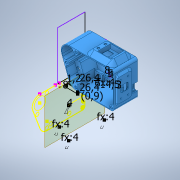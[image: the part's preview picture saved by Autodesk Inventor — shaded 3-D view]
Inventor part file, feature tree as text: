
AUTODESK INVENTOR PART (.ipt)
format: ipt  version: 2021.1 (Build 251245010, 245A)  size: 1,980,928 bytes
history: mixed  units: in
note: dims shown in document units (in); Inventor stores cm internally (conversion verified against a paired STEP export)
features: extrude x24, sketch x21, move_body x9, direct_edit x7, chamfer x6, projected_geometry x5, other x4, revolve x4, fillet x1, plane x1, imported_body x1
ambient origin geometry x8: Origin, YZ Plane, XZ Plane, XY Plane, X Axis, Y Axis, Z Axis, Center Point
bodies: Solid1 (imported_parasolid), Volumenkörper268 (imported_parasolid), Body1 (imported_parasolid)
feature tree (83):
  sketch  "Skizze1"  dims[d0=0.1575in d1=0.1575in]
  extrude  "Extrusion2"  Depth=0.1575in
  extrude  "Extrusion1"  Depth=0.1575in
  sketch  "Skizze3"  dims[d2=0.1575in d3=0.1575in]
  extrude  "Extrusion3"  Depth=0.252in TaperAngle=0.0deg
  extrude  "Extrusion4"  Depth=0.2756in TaperAngle=0.0deg
  extrude  "Extrusion5"  Depth=0.1575in
  extrude  "Extrusion6"  Depth=0.1575in
  direct_edit  "Direktbearbeitung2"
  extrude  "Extrusion8"  Depth=0.315in
  direct_edit  "Direktbearbeitung3"
  extrude  "Extrusion10"  Depth=0.1969in TaperAngle=0.0deg
  extrude  "Extrusion11"  TaperAngle=135.0deg  [1 undecoded]
  sketch  "Skizze16"  dims[d19=45.0deg d20=0.1969in d21=0.5906in d22=0.0in d23=0.0in]
  direct_edit  "Direktbearbeitung4"
  extrude  "Extrusion19"  TaperAngle=0.0deg  [1 undecoded]
  direct_edit  "Direktbearbeitung6"
  direct_edit  "Direktbearbeitung7"
  chamfer  "Fase2"  Distance=0.0157in
  extrude  "Extrusion26"  TaperAngle=135.0deg  [1 undecoded]
  chamfer  "Fase4"  Distance=0.3937in
  sketch  "Skizze29"  dims[d32=0.3937in d33=0.2362in d34=0.0in d35=0.0in d36=0.0in d37=0.0in d38=-0.0394in d39=0.0157in d40=0.0in]
  extrude  "Extrusion30"  TaperAngle=0.0deg  [1 undecoded]
  extrude  "Extrusion35"  Depth=0.3937in
  other  "Flächenverjüngung3"
  extrude  "Extrusion36"  Depth=0.0472in
  revolve  "Umdrehung1"
  sketch  "Skizze36"  dims[d45=0.3937in d46=0.0in d69=0.0in d70=0.0in d71=-0.2756in]
  fillet  "Rundung3"  Radius=0.315in
  extrude  "Extrusion37"  Depth=0.1181in TaperAngle=0.0deg
  chamfer  "Fase5"  [1 undecoded]
  plane  "Arbeitsebene2"
  extrude  "Extrusion38"  Depth=0.0197in
  extrude  "Extrusion39"  Depth=0.0197in
  extrude  "Extrusion40"  Depth=0.0197in TaperAngle=45.0deg
  chamfer  "Fase6"  Distance=0.0197in
  extrude  "Extrusion41"  Depth=0.1181in
  chamfer  "Fase7"  Distance=0.0197in
  extrude  "Extrusion42"  TaperAngle=90.0deg  [1 undecoded]
  extrude  "Extrusion9"  Depth=0.0787in
  direct_edit  "Direktbearbeitung8"
  sketch  "Skizze44"  dims[d122=0.0157in d123=0.0in d124=0.0197in d125=0.0787in d126=45.0deg d133=0.0197in d134=0.0in]
  sketch  "Skizze45"  dims[d144=0.3346in d145=0.0in d147=0.1181in]
  direct_edit  "Direktbearbeitung10"
  sketch  "Skizze47"  dims[d148=45.0deg d149=0.0197in d150=0.0in]
  extrude  "Extrusion43"  Depth=0.0787in TaperAngle=0.0deg
  extrude  "Extrusion44"  Depth=0.0787in TaperAngle=45.0deg
  chamfer  "Fase8"  Distance=0.3937in
  extrude  "Extrusion45"  Depth=0.0787in
  projected_geometry  "Projizierte Kontur2"
  sketch  "Skizze4"  dims[d4=0.1575in d5=0.252in d6=0.0in]
  sketch  "Skizze5"  dims[d7=0.2362in d8=0.0in d9=0.2756in d10=0.0in]
  sketch  "Skizze8"  dims[d11=0.1575in d12=0.0in d13=0.1575in]
  sketch  "Skizze9"  dims[d14=0.1575in d15=0.1575in]
  sketch  "Skizze10"  dims[d16=0.252in d17=0.0in d18=0.315in]
  sketch  "Skizze26"  dims[d30=0.315in d31=135.0deg]
  sketch  "Skizze35"  dims[d41=0.315in d42=135.0deg d43=0.3937in d44=0.0in]
  sketch  "Skizze37"  dims[d72=0.3937in d73=0.0in d74=1.0394in]
  projected_geometry  "Projizierte Kontur7"
  sketch  "Skizze38"  dims[d75=1.0394in d76=0.0472in d86=0.315in]
  sketch  "Skizze39"  dims[d87=0.2362in d88=0.0in d89=0.0in d90=0.1181in d104=0.0in d105=0.0in d106=-0.0787in]
  projected_geometry  "Projizierte Kontur8"
  sketch  "Skizze40"  dims[d109=0.0197in d113=0.0197in d114=0.0787in d115=45.0deg d119=0.0197in]
  projected_geometry  "Projizierte Kontur9"
  sketch  "Skizze41"  dims[d120=0.0197in d121=0.0197in]
  sketch  "Skizze48"  dims[d151=0.1969in d152=90.0deg d153=0.0787in d154=0.0787in d155=0.0in d156=0.0787in d157=0.0787in d158=45.0deg d159=0.3937in d160=0.0787in d161=1.9685in d162=0.0in d163=0.1969in d164=0.1969in d165=135.0deg d166=0.0394in d167=0.0in d168=0.1575in d172=0.1811in d173=0.252in d174=0.0in d175=0.0197in d176=0.0787in d177=45.0deg d178=0.1969in d179=0.1969in d180=0.0394in d181=0.0in d182=0.0197in d183=0.0787in d184=45.0deg d185=0.0157in d186=0.0in d187=-0.6184in d188=0.0in d189=2.8346in d190=0.0in d191=4.1339in d192=0.0in d193=0.0in d194=0.0in d195=0.0in d196=1.3346in d197=-1.0433in d198=0.0in d199=0.0in d201=180.0deg d202=3.9375in d203=0.1875in d204=0.375in d205=0.1575in d206=0.315in d207=0.3937in d208=0.0in d209=0.1969in d210=0.0354in d211=0.0in d212=0.0197in d213=0.0787in d214=45.0deg d215=0.2362in d216=0.0591in d217=0.0079in d218=0.0in d219=0.5709in d220=0.0354in d225=0.0687in]
  projected_geometry  "Projizierte Kontur11"
  other  "Löschen2"
  other  "Löschen3"
  move_body  "Verschieben1"
  other  "Löschen4"
  move_body  "Verschieben2"
  move_body  "Verschieben4"
  move_body  "Verschieben5"
  revolve  "Drehen1"  [1 undecoded]
  move_body  "Verschieben6"
  move_body  "Verschieben7"
  move_body  "Verschieben8"
  move_body  "Verschieben9"
  revolve  "Drehen3"  [1 undecoded]
  move_body  "Verschieben10"
  revolve  "Drehen4"  [1 undecoded]
  imported_body  NMx_Import_Brep_tag  [imported B-rep: ~163 faces, bbox_mm=[109.576773, 81.0, 48.4]]
note: 9 required parameter values undecoded (feature->parameter linkage not recoverable at this tier; creation-order binding heuristic only, values carry confidence <= 0.55)